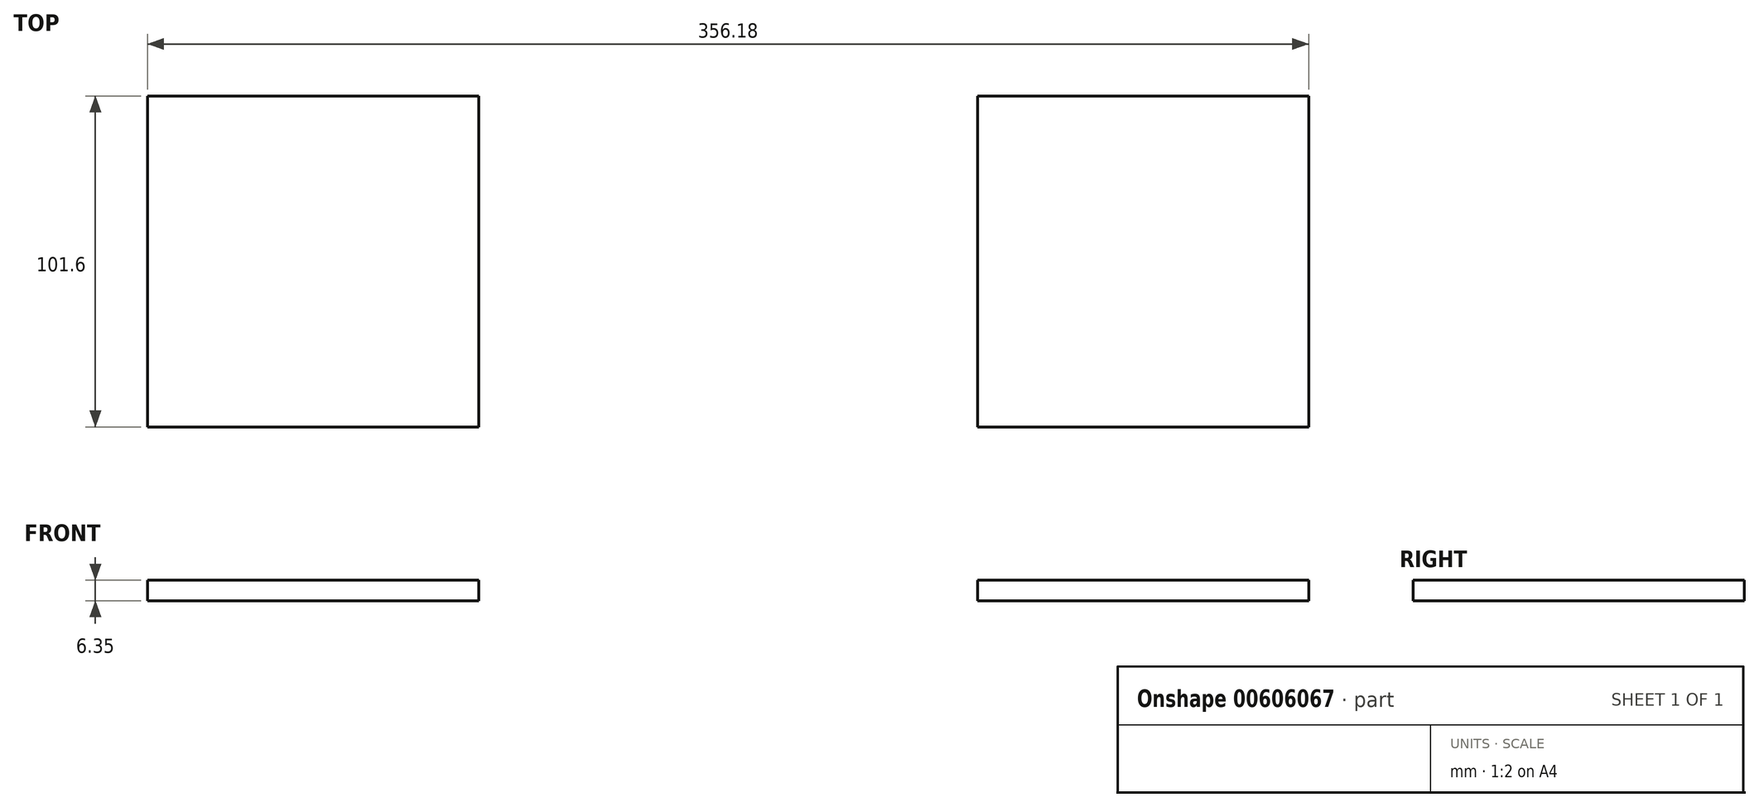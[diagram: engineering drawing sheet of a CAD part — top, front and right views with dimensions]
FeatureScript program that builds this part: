
annotation { "Feature Type Name" : "Feature", "Feature Type Description" : "" }
export const myFeature = defineFeature(function(context is Context, id is Id, definition is map)
    precondition{}
    {
        {
            var Q0;
            Q0=qCreatedBy(makeId("Top.planeOp"),FACE);
            var sketch = newSketch(context, id + "F0", { "sketchPlane" : qUnion([Q0])});
            skLineSegment(sketch, "E0", {"start": v(0, 0) * mm, "end": v(0, 101.6) * mm});
            skLineSegment(sketch, "E1", {"start": v(0, 101.6) * mm, "end": v(101.6, 101.6) * mm});
            skLineSegment(sketch, "E2", {"start": v(101.6, 101.6) * mm, "end": v(101.6, 0) * mm});
            skLineSegment(sketch, "E3", {"start": v(101.6, 0) * mm, "end": v(0, 0) * mm});
            skLineSegment(sketch, "E4", {"start": v(-76.49, 0) * mm, "end": v(-76.49, 77.03) * mm});
            skLineSegment(sketch, "E5.MirrorCS", {"start": v(-254.58, 0) * mm, "end": v(-152.98, 0) * mm});
            skLineSegment(sketch, "E6.MirrorCS", {"start": v(-254.58, 101.6) * mm, "end": v(-254.58, 0) * mm});
            skLineSegment(sketch, "E7.MirrorCS", {"start": v(-152.98, 101.6) * mm, "end": v(-254.58, 101.6) * mm});
            skLineSegment(sketch, "E8.MirrorCS", {"start": v(-152.98, 0) * mm, "end": v(-152.98, 101.6) * mm});
            skSolve(sketch);
        }
        {
            var Q0;
            Q0=makeQuery(id+"F0.imprint","IMPRINT",FACE,{"disambiguationData":[TD([[makeQuery(id+"F0.imprint","IMPRINT",EDGE,{"derivedFrom":sQuery(id+"F0.wireOp",EDGE,"E5.MirrorCS")}),1.0]])]});
            var Q1;
            Q1=makeQuery(id+"F0.imprint","IMPRINT",FACE,{"disambiguationData":[TD([[makeQuery(id+"F0.imprint","IMPRINT",EDGE,{"derivedFrom":sQuery(id+"F0.wireOp",EDGE,"E0")}),-1.0]])]});
            extrude(context, id + "F1", {"entities" : qUnion([Q0, Q1]), "depth" : 6.35 * mm, "offsetDistance" : 25.4 * mm});
        }
    });
